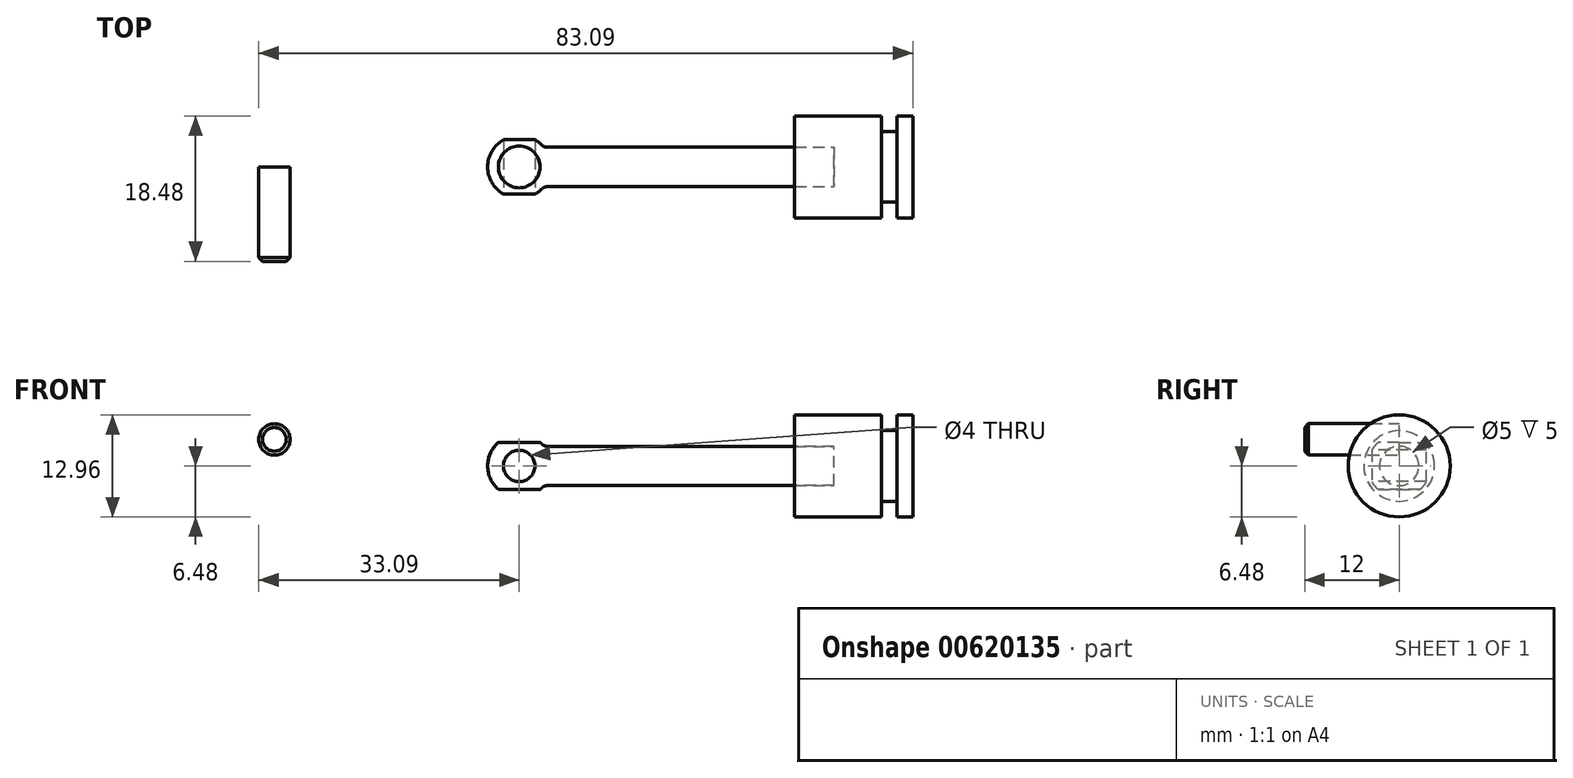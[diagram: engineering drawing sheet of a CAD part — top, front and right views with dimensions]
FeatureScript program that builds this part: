
annotation { "Feature Type Name" : "Feature", "Feature Type Description" : "" }
export const myFeature = defineFeature(function(context is Context, id is Id, definition is map)
    precondition{}
    {
        {
            var Q0;
            Q0=qCreatedBy(makeId("Front.planeOp"),FACE);
            var sketch = newSketch(context, id + "F0", { "sketchPlane" : qUnion([Q0])});
            skLineSegment(sketch, "E0", {"start": v(0, 0) * mm, "end": v(50.14, 0) * mm});
            skCircle(sketch, "E1", {"center": v(0, 0) * mm, "radius": 2 * mm});
            skLineSegment(sketch, "E2", {"start": v(35, 2.5) * mm, "end": v(35, -2.5) * mm});
            skPoint(sketch, "E3", {"position": v(35, 0) * mm});
            skLineSegment(sketch, "E4", {"start": v(35, 2.5) * mm, "end": v(3.12, 2.5) * mm});
            skLineSegment(sketch, "E5", {"start": v(35, -2.5) * mm, "end": v(3.12, -2.5) * mm});
            skLineSegment(sketch, "E6", {"start": v(-4, 3) * mm, "end": v(-4, -3) * mm, "construction": true});
            skPoint(sketch, "E7", {"position": v(-4, 0) * mm});
            skLineSegment(sketch, "E8", {"start": v(0, 0) * mm, "end": v(-4, 0) * mm});
            skLineSegment(sketch, "E9", {"start": v(-4, 3) * mm, "end": v(2.65, 3) * mm});
            skLineSegment(sketch, "E10", {"start": v(-4, -3) * mm, "end": v(2.65, -3) * mm});
            skArc(sketch, "E11", {"start": v(2.65, 3) * mm, "mid": v(0, 4) * mm, "end": v(-2.65, 3) * mm});
            skArc(sketch, "E12", {"start": v(2.65, -3) * mm, "mid": v(4, 0) * mm, "end": v(2.65, 3) * mm});
            skArc(sketch, "E13", {"start": v(-2.65, 3) * mm, "mid": v(-4, 0) * mm, "end": v(-2.65, -3) * mm});
            skArc(sketch, "E14", {"start": v(-2.65, -3) * mm, "mid": v(0, -4) * mm, "end": v(2.65, -3) * mm});
            skLineSegment(sketch, "E15", {"start": v(35, 2.5) * mm, "end": v(40, 2.5) * mm});
            skLineSegment(sketch, "E16", {"start": v(40, 2.5) * mm, "end": v(40, -2.5) * mm});
            skLineSegment(sketch, "E17", {"start": v(40, -2.5) * mm, "end": v(35, -2.5) * mm});
            skCircle(sketch, "E18", {"center": v(-31.1, 3.37) * mm, "radius": 2 * mm});
            skSolve(sketch);
        }
        {
            var Q0;
            {var subQ0=sQuery(id+"F0.wireOp",EDGE,"E11");Q0=makeQuery(id+"F0.imprint","IMPRINT",FACE,{"disambiguationData":[TD([[makeQuery(id+"F0.imprint","IMPRINT",EDGE,{"derivedFrom":subQ0}),1.0]])]});}
            var Q1;
            {var subQ6=sQuery(id+"F0.wireOp",EDGE,"E1");var subQ7=sQuery(id+"F0.wireOp",EDGE,"E0");var subQ8=makeQuery(id+"F0.imprint","INTERSECT",VERTEX,{"derivedFrom":[subQ7,subQ6]});Q1=makeQuery(id+"F0.imprint","IMPRINT",FACE,{"disambiguationData":[TD([[makeQuery(id+"F0.imprint","IMPRINT",EDGE,{"disambiguationData":[TD([[subQ8,-1.0]])],"derivedFrom":subQ7}),1.0]])]});}
            var Q2;
            {var subQ5=sQuery(id+"F0.wireOp",EDGE,"E4");Q2=makeQuery(id+"F0.imprint","IMPRINT",FACE,{"disambiguationData":[TD([[makeQuery(id+"F0.imprint","IMPRINT",EDGE,{"derivedFrom":subQ5}),1.0]])]});}
            var Q3;
            {var subQ0=sQuery(id+"F0.wireOp",EDGE,"E8");var subQ1=sQuery(id+"F0.wireOp",EDGE,"E0");var subQ2=makeQuery(id+"F0.imprint","INTERSECT",VERTEX,{"derivedFrom":[subQ1,subQ0]});Q3=makeQuery(id+"F0.imprint","IMPRINT",FACE,{"disambiguationData":[TD([[makeQuery(id+"F0.imprint","IMPRINT",EDGE,{"disambiguationData":[TD([[subQ2,-1.0]])],"derivedFrom":subQ1}),1.0]])]});}
            var Q4;
            {var subQ5=sQuery(id+"F0.wireOp",EDGE,"E15");Q4=makeQuery(id+"F0.imprint","IMPRINT",FACE,{"disambiguationData":[TD([[makeQuery(id+"F0.imprint","IMPRINT",EDGE,{"derivedFrom":subQ5}),-1.0]])]});}
            var Q5;
            Q5=sQuery(id+"F0.wireOp",EDGE,"E0");
            revolve(context, id + "F1", {"entities" : qUnion([Q0, Q1, Q2, Q3, Q4]), "axis" : qUnion([Q5]), "revolveType" : RevolveType.FULL});
        }
        {
            var Q0;
            {var subQ0=sQuery(id+"F0.wireOp",EDGE,"E11");Q0=makeQuery(id+"F0.imprint","IMPRINT",FACE,{"disambiguationData":[TD([[makeQuery(id+"F0.imprint","IMPRINT",EDGE,{"derivedFrom":subQ0}),1.0]])]});}
            var Q1;
            {var subQ0=sQuery(id+"F0.wireOp",EDGE,"E14");Q1=makeQuery(id+"F0.imprint","IMPRINT",FACE,{"disambiguationData":[TD([[makeQuery(id+"F0.imprint","IMPRINT",EDGE,{"derivedFrom":subQ0}),1.0]])]});}
            var Q2;
            {var subQ0=sQuery(id+"F0.wireOp",EDGE,"E8");var subQ1=sQuery(id+"F0.wireOp",EDGE,"E0");var subQ2=makeQuery(id+"F0.imprint","INTERSECT",VERTEX,{"derivedFrom":[subQ1,subQ0]});Q2=makeQuery(id+"F0.imprint","IMPRINT",FACE,{"disambiguationData":[TD([[makeQuery(id+"F0.imprint","IMPRINT",EDGE,{"disambiguationData":[TD([[subQ2,-1.0]])],"derivedFrom":subQ1}),1.0]])]});}
            var Q3;
            {var subQ0=sQuery(id+"F0.wireOp",EDGE,"E8");var subQ1=sQuery(id+"F0.wireOp",EDGE,"E0");var subQ2=makeQuery(id+"F0.imprint","INTERSECT",VERTEX,{"derivedFrom":[subQ1,subQ0]});Q3=makeQuery(id+"F0.imprint","IMPRINT",FACE,{"disambiguationData":[TD([[makeQuery(id+"F0.imprint","IMPRINT",EDGE,{"disambiguationData":[TD([[subQ2,-1.0]])],"derivedFrom":subQ1}),-1.0]])]});}
            extrude(context, id + "F2", {"entities" : qUnion([Q0, Q1, Q2, Q3]), "operationType" : NewBodyOperationType.REMOVE, "endBound" : BoundingType.SYMMETRIC, "oppositeDirection" : true, "depth" : 25 * mm, "offsetDistance" : 25 * mm});
        }
        {
            var Q0;
            Q0=makeQuery(id+"F1.opRevolve","SWEPT_EDGE",EDGE,{"disambiguationData":[OSD([sQuery(id+"F0.wireOp",EDGE,"E4"),sQuery(id+"F0.wireOp",EDGE,"E12")])]});
            fillet(context, id + "F3", {"entities" : qUnion([Q0]), "radius" : 1 * mm, "tangentPropagation" : true, "allowEdgeOverflow" : false});
        }
        {
            var Q0;
            Q0=qCreatedBy(makeId("Front.planeOp"),FACE);
            var sketch = newSketch(context, id + "F4", { "sketchPlane" : qUnion([Q0])});
            skLineSegment(sketch, "E19.0", {"start": v(35, 2.5) * mm, "end": v(35, -2.5) * mm});
            skLineSegment(sketch, "E20.0", {"start": v(40, -2.5) * mm, "end": v(35, -2.5) * mm});
            skLineSegment(sketch, "E21.0", {"start": v(35, 2.5) * mm, "end": v(40, 2.5) * mm});
            skLineSegment(sketch, "E22.0", {"start": v(40, 2.5) * mm, "end": v(40, -2.5) * mm});
            skLineSegment(sketch, "E23", {"start": v(35, -6.48) * mm, "end": v(35, 6.48) * mm});
            skPoint(sketch, "E24", {"position": v(35, 0) * mm});
            skPoint(sketch, "E25", {"position": v(40, 0) * mm});
            skLineSegment(sketch, "E26", {"start": v(35, -6.48) * mm, "end": v(50, -6.48) * mm});
            skLineSegment(sketch, "E27", {"start": v(50, -6.48) * mm, "end": v(50, 6.48) * mm});
            skLineSegment(sketch, "E28", {"start": v(50, 6.48) * mm, "end": v(35, 6.48) * mm});
            skLineSegment(sketch, "E29", {"start": v(48, -6.48) * mm, "end": v(48, 6.48) * mm});
            skLineSegment(sketch, "E30", {"start": v(46, -6.48) * mm, "end": v(46, 6.48) * mm});
            skLineSegment(sketch, "E31", {"start": v(50, 0) * mm, "end": v(35, 0) * mm});
            skLineSegment(sketch, "E32", {"start": v(48, -4.48) * mm, "end": v(46, -4.48) * mm});
            skLineSegment(sketch, "E33.MirrorCS", {"start": v(48, 4.48) * mm, "end": v(46, 4.48) * mm});
            skSolve(sketch);
        }
        {
            var Q0;
            {var subQ1=sQuery(id+"F4.wireOp",EDGE,"E28");var subQ6=sQuery(id+"F4.wireOp",EDGE,"E27");var subQ7=makeQuery(id+"F4.imprint","INTERSECT",VERTEX,{"derivedFrom":[subQ6,subQ1]});Q0=makeQuery(id+"F4.imprint","IMPRINT",FACE,{"disambiguationData":[TD([[makeQuery(id+"F4.imprint","IMPRINT",EDGE,{"disambiguationData":[TD([[subQ7,1.0]])],"derivedFrom":subQ6}),1.0]])]});}
            var Q1;
            {var subQ0=sQuery(id+"F4.wireOp",EDGE,"E33.MirrorCS");Q1=makeQuery(id+"F4.imprint","IMPRINT",FACE,{"disambiguationData":[TD([[makeQuery(id+"F4.imprint","IMPRINT",EDGE,{"derivedFrom":subQ0}),1.0]])]});}
            var Q2;
            {var subQ9=sQuery(id+"F4.wireOp",EDGE,"E21.0");Q2=makeQuery(id+"F4.imprint","IMPRINT",FACE,{"disambiguationData":[TD([[makeQuery(id+"F4.imprint","IMPRINT",EDGE,{"derivedFrom":subQ9}),1.0]])]});}
            var Q3;
            Q3=sQuery(id+"F4.wireOp",EDGE,"E31");
            revolve(context, id + "F5", {"entities" : qUnion([Q0, Q1, Q2]), "axis" : qUnion([Q3]), "revolveType" : RevolveType.FULL});
        }
        {
            var Q0;
            Q0=makeQuery(id+"F0.imprint","IMPRINT",FACE,{"disambiguationData":[TD([[makeQuery(id+"F0.imprint","IMPRINT",EDGE,{"derivedFrom":sQuery(id+"F0.wireOp",EDGE,"E18")}),1.0]])]});
            extrude(context, id + "F6", {"entities" : qUnion([Q0]), "depth" : 12 * mm, "offsetDistance" : 25 * mm});
        }
        {
            var Q0;
            Q0=makeQuery(id+"F6.opExtrude","CAP_EDGE",EDGE,{"disambiguationData":[OSD([sQuery(id+"F0.wireOp",EDGE,"E18")])],"isStart":false});
            chamfer(context, id + "F7", {"entities" : qUnion([Q0]), "width" : .5 * mm, "tangentPropagation" : true});
        }
    });
